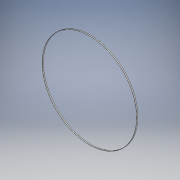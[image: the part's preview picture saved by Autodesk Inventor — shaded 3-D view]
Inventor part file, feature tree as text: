
AUTODESK INVENTOR PART (.ipt)
format: ipt  version: 2019 (Build 230136000, 136)  size: 105,472 bytes
history: native  units: mm
features: extrude x2, sketch x2
ambient origin geometry x8: Origin, YZ Plane, XZ Plane, XY Plane, X Axis, Y Axis, Z Axis, Center Point
bodies: Solid1 (feature_tree)
feature tree (4):
  extrude  "Extrusion1"  Depth=5.0mm TaperAngle=0.0deg
  extrude  "Extrusion2"  Depth=0.27mm TaperAngle=0.0deg
  sketch  "Sketch1"  dims[d0=415.34mm d1=5.0mm d2=0.0mm]
  sketch  "Sketch2"  dims[d3=414.0mm d4=0.27mm d5=0.0mm]
